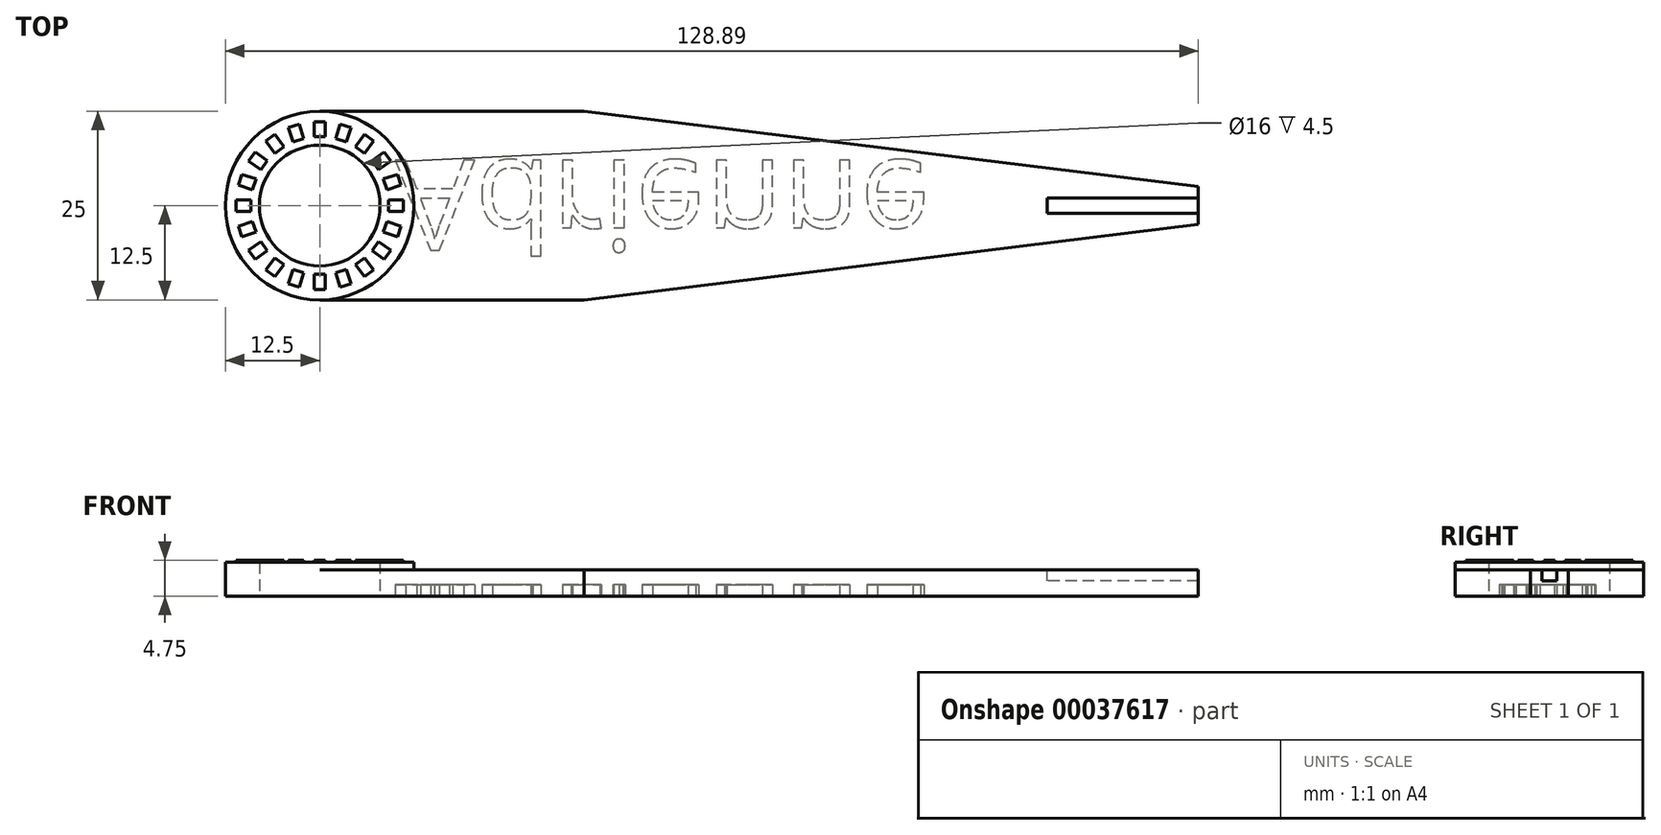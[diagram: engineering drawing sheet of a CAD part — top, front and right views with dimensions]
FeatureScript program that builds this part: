
annotation { "Feature Type Name" : "Feature", "Feature Type Description" : "" }
export const myFeature = defineFeature(function(context is Context, id is Id, definition is map)
    precondition{}
    {
        {
            var Q0;
            Q0=qCreatedBy(makeId("Top.planeOp"),FACE);
            var sketch = newSketch(context, id + "F0", { "sketchPlane" : qUnion([Q0])});
            skArc(sketch, "E0", {"start": v(0, 12.5) * mm, "mid": v(-12.5, 0) * mm, "end": v(0, -12.5) * mm});
            skCircle(sketch, "E1", {"center": v(0, 0) * mm, "radius": 8 * mm});
            skLineSegment(sketch, "E2", {"start": v(0, 12.5) * mm, "end": v(35, 12.5) * mm});
            skLineSegment(sketch, "E3", {"start": v(35, 12.5) * mm, "end": v(116.39, 2.5) * mm});
            skLineSegment(sketch, "E4", {"start": v(1.48, 0) * mm, "end": v(33.07, 0) * mm, "construction": true});
            skLineSegment(sketch, "E5", {"start": v(35, 12.5) * mm, "end": v(71.86, 12.5) * mm, "construction": true});
            skLineSegment(sketch, "E6.MirrorCS", {"start": v(0, -12.5) * mm, "end": v(35, -12.5) * mm});
            skLineSegment(sketch, "E7.MirrorCS", {"start": v(35, -12.5) * mm, "end": v(116.39, -2.5) * mm});
            skLineSegment(sketch, "E8", {"start": v(116.39, 2.5) * mm, "end": v(116.39, -2.5) * mm});
            skSolve(sketch);
        }
        {
            var Q0;
            Q0 = qSketchRegion(id + "F0", true);
            extrude(context, id + "F1", {"entities" : qUnion([Q0]), "depth" : 3.5 * mm});
        }
        {
            var Q0;
            Q0=makeQuery(id+"F1.opExtrude","CAP_FACE",FACE,{"disambiguationData":[OSD([sQuery(id+"F0.wireOp",EDGE,"E0"),sQuery(id+"F0.wireOp",EDGE,"E1"),sQuery(id+"F0.wireOp",EDGE,"E2"),sQuery(id+"F0.wireOp",EDGE,"E3"),sQuery(id+"F0.wireOp",EDGE,"E6.MirrorCS"),sQuery(id+"F0.wireOp",EDGE,"E7.MirrorCS"),sQuery(id+"F0.wireOp",EDGE,"E8")])],"isStart":false});
            var sketch = newSketch(context, id + "F2", { "sketchPlane" : qUnion([Q0])});
            skCircle(sketch, "E9", {"center": v(0, 0) * mm, "radius": 12.5 * mm});
            skCircle(sketch, "E10", {"center": v(0, 0) * mm, "radius": 8 * mm});
            skSolve(sketch);
        }
        {
            var Q0;
            Q0 = qSketchRegion(id + "F2", true);
            extrude(context, id + "F3", {"entities" : qUnion([Q0]), "operationType" : NewBodyOperationType.ADD, "depth" : 1 * mm});
        }
        {
            var Q0;
            Q0=makeQuery(id+"F3.opExtrude","CAP_FACE",FACE,{"disambiguationData":[OSD([sQuery(id+"F2.wireOp",EDGE,"E9"),sQuery(id+"F2.wireOp",EDGE,"E10")])],"isStart":false});
            var sketch = newSketch(context, id + "F4", { "sketchPlane" : qUnion([Q0])});
            skLineSegment(sketch, "E11.bottom", {"start": v(-0.75, 11.1) * mm, "end": v(0.75, 11.1) * mm});
            skLineSegment(sketch, "E11.top", {"start": v(-0.75, 9.1) * mm, "end": v(0.75, 9.1) * mm});
            skLineSegment(sketch, "E11.left", {"start": v(-0.75, 11.1) * mm, "end": v(-0.75, 9.1) * mm});
            skLineSegment(sketch, "E11.right", {"start": v(0.75, 11.1) * mm, "end": v(0.75, 9.1) * mm});
            skLineSegment(sketch, "E12.1.0", {"start": v(-2.72, 10.8) * mm, "end": v(-2.1, 8.9) * mm});
            skLineSegment(sketch, "E12.1.1", {"start": v(-4.14, 10.33) * mm, "end": v(-2.72, 10.8) * mm});
            skLineSegment(sketch, "E12.1.2", {"start": v(-4.14, 10.33) * mm, "end": v(-3.53, 8.43) * mm});
            skLineSegment(sketch, "E12.1.3", {"start": v(-3.53, 8.43) * mm, "end": v(-2.1, 8.9) * mm});
            skLineSegment(sketch, "E12.2.0", {"start": v(-5.92, 9.42) * mm, "end": v(-4.74, 7.8) * mm});
            skLineSegment(sketch, "E12.2.1", {"start": v(-7.13, 8.54) * mm, "end": v(-5.92, 9.42) * mm});
            skLineSegment(sketch, "E12.2.2", {"start": v(-7.13, 8.54) * mm, "end": v(-5.96, 6.92) * mm});
            skLineSegment(sketch, "E12.2.3", {"start": v(-5.96, 6.92) * mm, "end": v(-4.74, 7.8) * mm});
            skLineSegment(sketch, "E12.3.0", {"start": v(-8.54, 7.13) * mm, "end": v(-6.92, 5.96) * mm});
            skLineSegment(sketch, "E12.3.1", {"start": v(-9.42, 5.92) * mm, "end": v(-8.54, 7.13) * mm});
            skLineSegment(sketch, "E12.3.2", {"start": v(-9.42, 5.92) * mm, "end": v(-7.8, 4.74) * mm});
            skLineSegment(sketch, "E12.3.3", {"start": v(-7.8, 4.74) * mm, "end": v(-6.92, 5.96) * mm});
            skLineSegment(sketch, "E12.4.0", {"start": v(-10.33, 4.14) * mm, "end": v(-8.43, 3.53) * mm});
            skLineSegment(sketch, "E12.4.1", {"start": v(-10.8, 2.72) * mm, "end": v(-10.33, 4.14) * mm});
            skLineSegment(sketch, "E12.4.2", {"start": v(-10.8, 2.72) * mm, "end": v(-8.9, 2.1) * mm});
            skLineSegment(sketch, "E12.4.3", {"start": v(-8.9, 2.1) * mm, "end": v(-8.43, 3.53) * mm});
            skLineSegment(sketch, "E12.5.0", {"start": v(-11.1, 0.75) * mm, "end": v(-9.1, 0.75) * mm});
            skLineSegment(sketch, "E12.5.1", {"start": v(-11.1, -0.75) * mm, "end": v(-11.1, 0.75) * mm});
            skLineSegment(sketch, "E12.5.2", {"start": v(-11.1, -0.75) * mm, "end": v(-9.1, -0.75) * mm});
            skLineSegment(sketch, "E12.5.3", {"start": v(-9.1, -0.75) * mm, "end": v(-9.1, 0.75) * mm});
            skLineSegment(sketch, "E12.6.0", {"start": v(-10.8, -2.72) * mm, "end": v(-8.9, -2.1) * mm});
            skLineSegment(sketch, "E12.6.1", {"start": v(-10.33, -4.14) * mm, "end": v(-10.8, -2.72) * mm});
            skLineSegment(sketch, "E12.6.2", {"start": v(-10.33, -4.14) * mm, "end": v(-8.43, -3.53) * mm});
            skLineSegment(sketch, "E12.6.3", {"start": v(-8.43, -3.53) * mm, "end": v(-8.9, -2.1) * mm});
            skLineSegment(sketch, "E12.7.0", {"start": v(-9.42, -5.92) * mm, "end": v(-7.8, -4.74) * mm});
            skLineSegment(sketch, "E12.7.1", {"start": v(-8.54, -7.13) * mm, "end": v(-9.42, -5.92) * mm});
            skLineSegment(sketch, "E12.7.2", {"start": v(-8.54, -7.13) * mm, "end": v(-6.92, -5.96) * mm});
            skLineSegment(sketch, "E12.7.3", {"start": v(-6.92, -5.96) * mm, "end": v(-7.8, -4.74) * mm});
            skLineSegment(sketch, "E12.8.0", {"start": v(-7.13, -8.54) * mm, "end": v(-5.96, -6.92) * mm});
            skLineSegment(sketch, "E12.8.1", {"start": v(-5.92, -9.42) * mm, "end": v(-7.13, -8.54) * mm});
            skLineSegment(sketch, "E12.8.2", {"start": v(-5.92, -9.42) * mm, "end": v(-4.74, -7.8) * mm});
            skLineSegment(sketch, "E12.8.3", {"start": v(-4.74, -7.8) * mm, "end": v(-5.96, -6.92) * mm});
            skLineSegment(sketch, "E12.9.0", {"start": v(-4.14, -10.33) * mm, "end": v(-3.53, -8.43) * mm});
            skLineSegment(sketch, "E12.9.1", {"start": v(-2.72, -10.8) * mm, "end": v(-4.14, -10.33) * mm});
            skLineSegment(sketch, "E12.9.2", {"start": v(-2.72, -10.8) * mm, "end": v(-2.1, -8.9) * mm});
            skLineSegment(sketch, "E12.9.3", {"start": v(-2.1, -8.9) * mm, "end": v(-3.53, -8.43) * mm});
            skLineSegment(sketch, "E12.10.0", {"start": v(-0.75, -11.1) * mm, "end": v(-0.75, -9.1) * mm});
            skLineSegment(sketch, "E12.10.1", {"start": v(0.75, -11.1) * mm, "end": v(-0.75, -11.1) * mm});
            skLineSegment(sketch, "E12.10.2", {"start": v(0.75, -11.1) * mm, "end": v(0.75, -9.1) * mm});
            skLineSegment(sketch, "E12.10.3", {"start": v(0.75, -9.1) * mm, "end": v(-0.75, -9.1) * mm});
            skLineSegment(sketch, "E12.11.0", {"start": v(2.72, -10.8) * mm, "end": v(2.1, -8.9) * mm});
            skLineSegment(sketch, "E12.11.1", {"start": v(4.14, -10.33) * mm, "end": v(2.72, -10.8) * mm});
            skLineSegment(sketch, "E12.11.2", {"start": v(4.14, -10.33) * mm, "end": v(3.53, -8.43) * mm});
            skLineSegment(sketch, "E12.11.3", {"start": v(3.53, -8.43) * mm, "end": v(2.1, -8.9) * mm});
            skLineSegment(sketch, "E12.12.0", {"start": v(5.92, -9.42) * mm, "end": v(4.74, -7.8) * mm});
            skLineSegment(sketch, "E12.12.1", {"start": v(7.13, -8.54) * mm, "end": v(5.92, -9.42) * mm});
            skLineSegment(sketch, "E12.12.2", {"start": v(7.13, -8.54) * mm, "end": v(5.96, -6.92) * mm});
            skLineSegment(sketch, "E12.12.3", {"start": v(5.96, -6.92) * mm, "end": v(4.74, -7.8) * mm});
            skLineSegment(sketch, "E12.13.0", {"start": v(8.54, -7.13) * mm, "end": v(6.92, -5.96) * mm});
            skLineSegment(sketch, "E12.13.1", {"start": v(9.42, -5.92) * mm, "end": v(8.54, -7.13) * mm});
            skLineSegment(sketch, "E12.13.2", {"start": v(9.42, -5.92) * mm, "end": v(7.8, -4.74) * mm});
            skLineSegment(sketch, "E12.13.3", {"start": v(7.8, -4.74) * mm, "end": v(6.92, -5.96) * mm});
            skLineSegment(sketch, "E12.14.0", {"start": v(10.33, -4.14) * mm, "end": v(8.43, -3.53) * mm});
            skLineSegment(sketch, "E12.14.1", {"start": v(10.8, -2.72) * mm, "end": v(10.33, -4.14) * mm});
            skLineSegment(sketch, "E12.14.2", {"start": v(10.8, -2.72) * mm, "end": v(8.9, -2.1) * mm});
            skLineSegment(sketch, "E12.14.3", {"start": v(8.9, -2.1) * mm, "end": v(8.43, -3.53) * mm});
            skLineSegment(sketch, "E12.15.0", {"start": v(11.1, -0.75) * mm, "end": v(9.1, -0.75) * mm});
            skLineSegment(sketch, "E12.15.1", {"start": v(11.1, 0.75) * mm, "end": v(11.1, -0.75) * mm});
            skLineSegment(sketch, "E12.15.2", {"start": v(11.1, 0.75) * mm, "end": v(9.1, 0.75) * mm});
            skLineSegment(sketch, "E12.15.3", {"start": v(9.1, 0.75) * mm, "end": v(9.1, -0.75) * mm});
            skLineSegment(sketch, "E12.16.0", {"start": v(10.8, 2.72) * mm, "end": v(8.9, 2.1) * mm});
            skLineSegment(sketch, "E12.16.1", {"start": v(10.33, 4.14) * mm, "end": v(10.8, 2.72) * mm});
            skLineSegment(sketch, "E12.16.2", {"start": v(10.33, 4.14) * mm, "end": v(8.43, 3.53) * mm});
            skLineSegment(sketch, "E12.16.3", {"start": v(8.43, 3.53) * mm, "end": v(8.9, 2.1) * mm});
            skLineSegment(sketch, "E12.17.0", {"start": v(9.42, 5.92) * mm, "end": v(7.8, 4.74) * mm});
            skLineSegment(sketch, "E12.17.1", {"start": v(8.54, 7.13) * mm, "end": v(9.42, 5.92) * mm});
            skLineSegment(sketch, "E12.17.2", {"start": v(8.54, 7.13) * mm, "end": v(6.92, 5.96) * mm});
            skLineSegment(sketch, "E12.17.3", {"start": v(6.92, 5.96) * mm, "end": v(7.8, 4.74) * mm});
            skLineSegment(sketch, "E12.18.0", {"start": v(7.13, 8.54) * mm, "end": v(5.96, 6.92) * mm});
            skLineSegment(sketch, "E12.18.1", {"start": v(5.92, 9.42) * mm, "end": v(7.13, 8.54) * mm});
            skLineSegment(sketch, "E12.18.2", {"start": v(5.92, 9.42) * mm, "end": v(4.74, 7.8) * mm});
            skLineSegment(sketch, "E12.18.3", {"start": v(4.74, 7.8) * mm, "end": v(5.96, 6.92) * mm});
            skLineSegment(sketch, "E12.19.0", {"start": v(4.14, 10.33) * mm, "end": v(3.53, 8.43) * mm});
            skLineSegment(sketch, "E12.19.1", {"start": v(2.72, 10.8) * mm, "end": v(4.14, 10.33) * mm});
            skLineSegment(sketch, "E12.19.2", {"start": v(2.72, 10.8) * mm, "end": v(2.1, 8.9) * mm});
            skLineSegment(sketch, "E12.19.3", {"start": v(2.1, 8.9) * mm, "end": v(3.53, 8.43) * mm});
            skPoint(sketch, "E12.center", {"position": v(0, 0) * mm});
            skSolve(sketch);
        }
        {
            var Q0;
            Q0 = qSketchRegion(id + "F4", true);
            extrude(context, id + "F5", {"entities" : qUnion([Q0]), "operationType" : NewBodyOperationType.ADD, "depth" : .25 * mm});
        }
        {
            var Q0;
            Q0=makeQuery(id+"F1.opExtrude","CAP_FACE",FACE,{"disambiguationData":[OSD([sQuery(id+"F0.wireOp",EDGE,"E0"),sQuery(id+"F0.wireOp",EDGE,"E1"),sQuery(id+"F0.wireOp",EDGE,"E2"),sQuery(id+"F0.wireOp",EDGE,"E3"),sQuery(id+"F0.wireOp",EDGE,"E6.MirrorCS"),sQuery(id+"F0.wireOp",EDGE,"E7.MirrorCS"),sQuery(id+"F0.wireOp",EDGE,"E8")])],"isStart":false});
            var sketch = newSketch(context, id + "F6", { "sketchPlane" : qUnion([Q0])});
            skLineSegment(sketch, "E13.bottom", {"start": v(116.39, 1) * mm, "end": v(96.39, 1) * mm});
            skLineSegment(sketch, "E13.top", {"start": v(116.39, -1) * mm, "end": v(96.39, -1) * mm});
            skLineSegment(sketch, "E13.left", {"start": v(116.39, 1) * mm, "end": v(116.39, -1) * mm});
            skLineSegment(sketch, "E13.right", {"start": v(96.39, 1) * mm, "end": v(96.39, -1) * mm});
            skSolve(sketch);
        }
        {
            var Q0;
            Q0 = qSketchRegion(id + "F6", true);
            extrude(context, id + "F7", {"entities" : qUnion([Q0]), "operationType" : NewBodyOperationType.REMOVE, "oppositeDirection" : true, "depth" : 1.5 * mm});
        }
        {
            var Q0;
            Q0=makeQuery(id+"F1.opExtrude","CAP_EDGE",EDGE,{"disambiguationData":[OSD([sQuery(id+"F0.wireOp",EDGE,"E6.MirrorCS")])],"isStart":true});
            cPlane(context, id + "F8", {"entities" : qUnion([Q0]), "cplaneType" : CPlaneType.LINE_ANGLE, "offset" : 150 * mm, "angle" : 270 * degree, "width" : 150 * mm, "height" : 150 * mm});
        }
        {
            var Q0;
            Q0=qCreatedBy(id+"F8.planeOp",FACE);
            var sketch = newSketch(context, id + "F9", { "sketchPlane" : qUnion([Q0])});
            skText(sketch, "E14", { "text": "Adrienne", "fontName": "OpenSans-Regular.ttf"});
            skPoint(sketch, "E15", {"position": v(10, 0) * mm});
            skLineSegment(sketch, "E16", {"start": v(0, 0) * mm, "end": v(35.85, 0) * mm, "construction": true});
            const initialGuessF9  = {"E14": [0.01, -0.006, 1, 0, 0.01199]};
            skSetInitialGuess(sketch, initialGuessF9);
            skSolve(sketch);
        }
        {
            var Q0;
            Q0 = qSketchRegion(id + "F9", true);
            extrude(context, id + "F10", {"entities" : qUnion([Q0]), "operationType" : NewBodyOperationType.REMOVE, "oppositeDirection" : true, "depth" : 1.5 * mm});
        }
    });
